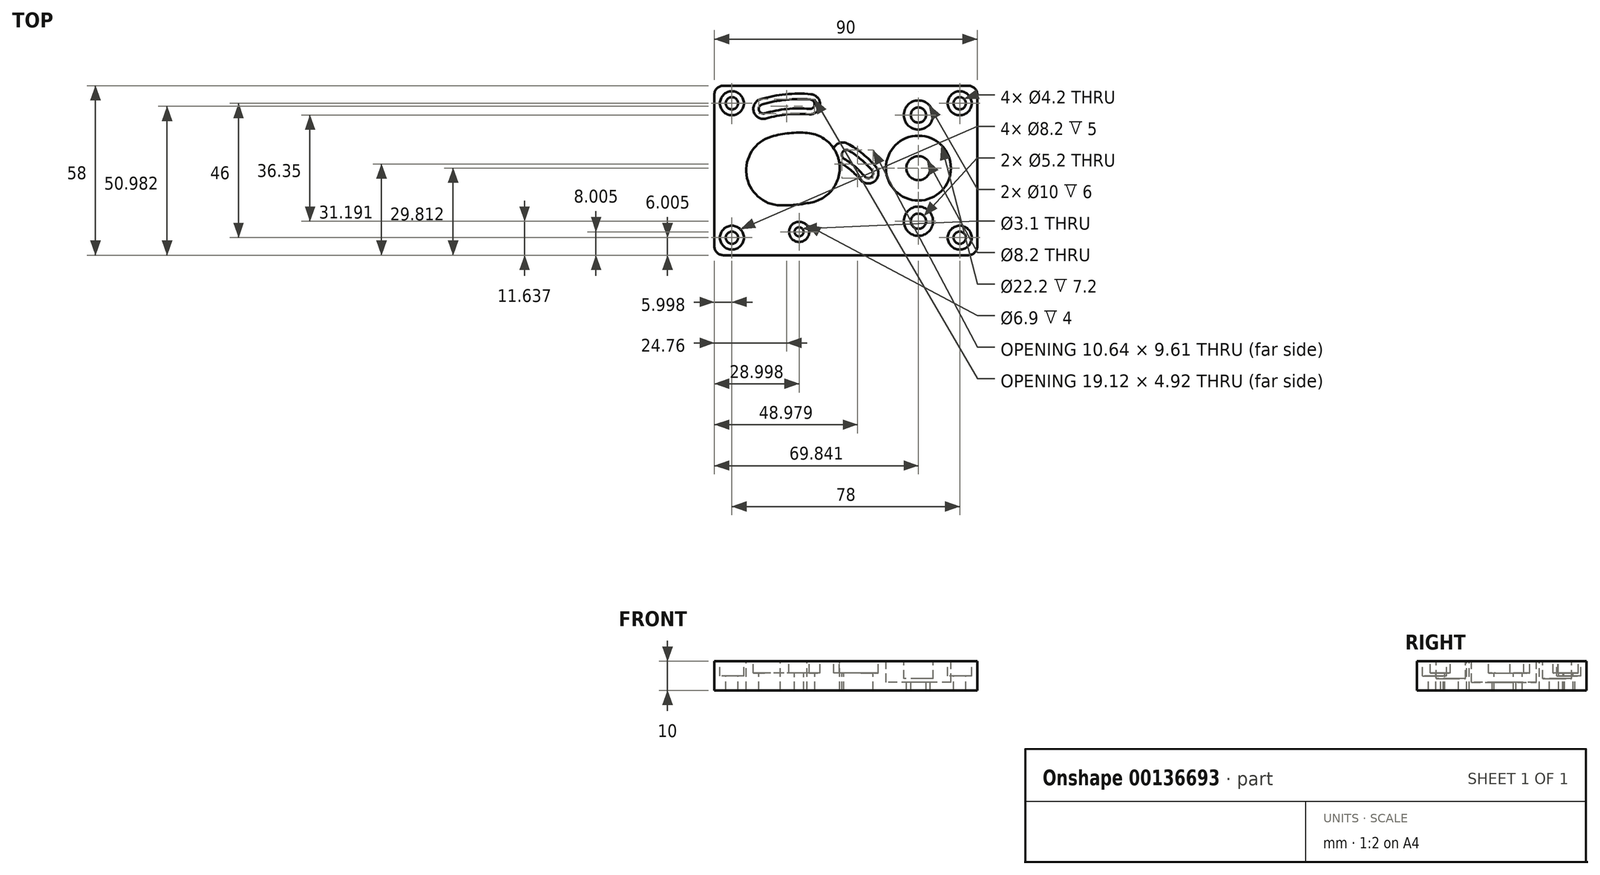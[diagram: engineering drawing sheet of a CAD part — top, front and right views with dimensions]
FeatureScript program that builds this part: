
annotation { "Feature Type Name" : "Feature", "Feature Type Description" : "" }
export const myFeature = defineFeature(function(context is Context, id is Id, definition is map)
    precondition{}
    {
        {
            var Q0;
            Q0=qCreatedBy(makeId("Top.planeOp"),FACE);
            var sketch = newSketch(context, id + "F0", { "sketchPlane" : qUnion([Q0])});
            skLineSegment(sketch, "E0.right", {"start": v(40.3, 23.5) * mm, "end": v(40.3, -28.5) * mm});
            skCircle(sketch, "E1", {"center": v(-20.7, -23.5) * mm, "radius": 1.55 * mm});
            skArc(sketch, "E2", {"start": v(-33.36, 20.15) * mm, "mid": v(-34.45, 18.16) * mm, "end": v(-32.47, 17.07) * mm});
            skArc(sketch, "E3", {"start": v(-17.1, 18.6) * mm, "mid": v(-15.38, 20.05) * mm, "end": v(-16.84, 21.78) * mm});
            skLineSegment(sketch, "E4", {"start": v(-21.13, -22) * mm, "end": v(-20.7, -23.5) * mm});
            skLineSegment(sketch, "E5", {"start": v(-20.7, -23.5) * mm, "end": v(-20.57, -21.95) * mm});
            skArc(sketch, "E6", {"start": v(-17.1, 18.6) * mm, "mid": v(-24.86, 18.54) * mm, "end": v(-32.47, 17.07) * mm});
            skArc(sketch, "E7", {"start": v(-16.84, 21.78) * mm, "mid": v(-25.17, 21.72) * mm, "end": v(-33.36, 20.15) * mm});
            skPoint(sketch, "E8", {"position": v(-22.86, -1.69) * mm});
            skLineSegment(sketch, "E9.trimOffspring", {"start": v(-20.85, -21.95) * mm, "end": v(-20.7, -23.5) * mm});
            skPoint(sketch, "E10.start.orphan", {"position": v(-25.01, 20.12) * mm});
            skArc(sketch, "E11.0", {"start": v(-16.68, 23.62) * mm, "mid": v(-25.35, 23.57) * mm, "end": v(-33.87, 21.92) * mm});
            skArc(sketch, "E11.1", {"start": v(-17.27, 16.75) * mm, "mid": v(-13.54, 19.9) * mm, "end": v(-16.68, 23.62) * mm});
            skArc(sketch, "E11.2", {"start": v(-17.27, 16.75) * mm, "mid": v(-24.68, 16.7) * mm, "end": v(-31.95, 15.3) * mm});
            skArc(sketch, "E11.3", {"start": v(-33.87, 21.92) * mm, "mid": v(-36.23, 17.65) * mm, "end": v(-31.95, 15.3) * mm});
            skLineSegment(sketch, "E12.anchor2", {"start": v(-22.86, -1.69) * mm, "end": v(-44.67, -3.84) * mm, "construction": true});
            skCircle(sketch, "E13", {"center": v(-20.7, -23.5) * mm, "radius": 3.45 * mm});
            skArc(sketch, "E14", {"start": v(-30.15, 9.08) * mm, "mid": v(-38.7, -4) * mm, "end": v(-27.06, -14.44) * mm});
            skArc(sketch, "E15", {"start": v(-17.81, 10.33) * mm, "mid": v(-24.04, 10.3) * mm, "end": v(-30.15, 9.08) * mm});
            skArc(sketch, "E16", {"start": v(-27.06, -14.44) * mm, "mid": v(-22.5, -14.31) * mm, "end": v(-18, -13.65) * mm});
            skPoint(sketch, "E17.center.orphan", {"position": v(-17.7, -1.69) * mm});
            skArc(sketch, "E18.trimOffspring", {"start": v(-18, -13.65) * mm, "mid": v(-6.81, -1.75) * mm, "end": v(-17.81, 10.33) * mm});
            skLineSegment(sketch, "E19", {"start": v(-22.86, -1.69) * mm, "end": v(50.56, -1.69) * mm, "construction": true});
            skCircle(sketch, "E20", {"center": v(20.14, -1.69) * mm, "radius": 4.1 * mm});
            skCircle(sketch, "E21", {"center": v(20.14, -1.69) * mm, "radius": 11.1 * mm});
            skLineSegment(sketch, "E22", {"start": v(-49.7, 23.5) * mm, "end": v(-49.7, -28.5) * mm});
            skLineSegment(sketch, "E23", {"start": v(37.3, 26.5) * mm, "end": v(-46.7, 26.5) * mm});
            skLineSegment(sketch, "E24", {"start": v(37.3, -31.5) * mm, "end": v(-46.7, -31.5) * mm});
            skLineSegment(sketch, "E25", {"start": v(-22.86, -1.69) * mm, "end": v(-55.16, -1.69) * mm, "construction": true});
            skCircle(sketch, "E26", {"center": v(-43.7, 20.5) * mm, "radius": 2.1 * mm});
            skCircle(sketch, "E27", {"center": v(34.3, 20.5) * mm, "radius": 2.1 * mm});
            skCircle(sketch, "E28", {"center": v(-43.7, -25.5) * mm, "radius": 2.1 * mm});
            skCircle(sketch, "E29", {"center": v(34.3, -25.5) * mm, "radius": 2.1 * mm});
            skPoint(sketch, "E30.visualSharp", {"position": v(-49.7, 26.5) * mm});
            skArc(sketch, "E30.filletArc", {"start": v(-46.7, 26.5) * mm, "mid": v(-48.82, 25.63) * mm, "end": v(-49.7, 23.5) * mm});
            skPoint(sketch, "E31.visualSharp", {"position": v(-49.7, -31.5) * mm});
            skArc(sketch, "E31.filletArc", {"start": v(-49.7, -28.5) * mm, "mid": v(-48.82, -30.62) * mm, "end": v(-46.7, -31.5) * mm});
            skPoint(sketch, "E32.visualSharp", {"position": v(40.3, -31.5) * mm});
            skArc(sketch, "E32.filletArc", {"start": v(37.3, -31.5) * mm, "mid": v(39.42, -30.62) * mm, "end": v(40.3, -28.5) * mm});
            skPoint(sketch, "E33.visualSharp", {"position": v(40.3, 26.5) * mm});
            skArc(sketch, "E33.filletArc", {"start": v(40.3, 23.5) * mm, "mid": v(39.42, 25.63) * mm, "end": v(37.3, 26.5) * mm});
            skCircle(sketch, "E34", {"center": v(-43.7, 20.5) * mm, "radius": 4.1 * mm});
            skCircle(sketch, "E35", {"center": v(-43.7, -25.5) * mm, "radius": 4.1 * mm});
            skCircle(sketch, "E36", {"center": v(34.3, -25.5) * mm, "radius": 4.1 * mm});
            skCircle(sketch, "E37", {"center": v(34.3, 20.5) * mm, "radius": 4.1 * mm});
            skLineSegment(sketch, "E38", {"start": v(-20.7, -23.5) * mm, "end": v(-16.97, 20.19) * mm, "construction": true});
            skLineSegment(sketch, "E39", {"start": v(-20.7, -23.5) * mm, "end": v(-32.91, 18.61) * mm, "construction": true});
            skLineSegment(sketch, "E40", {"start": v(-18.84, -1.65) * mm, "end": v(5.84, -3.76) * mm, "construction": true});
            skLineSegment(sketch, "E41", {"start": v(-26.8, -2.44) * mm, "end": v(-1.4, 4.93) * mm, "construction": true});
            skArc(sketch, "E42", {"start": v(1.78, -4.55) * mm, "mid": v(4.04, -4.74) * mm, "end": v(4.23, -2.49) * mm});
            skLineSegment(sketch, "E43", {"start": v(-20.7, -23.5) * mm, "end": v(-5.75, 3.66) * mm, "construction": true});
            skLineSegment(sketch, "E44", {"start": v(3, -3.52) * mm, "end": v(-20.7, -23.5) * mm, "construction": true});
            skLineSegment(sketch, "E45", {"start": v(-5.75, 3.66) * mm, "end": v(-1.87, 10.71) * mm, "construction": true});
            skLineSegment(sketch, "E46", {"start": v(3, -3.52) * mm, "end": v(8.43, 1.05) * mm, "construction": true});
            skArc(sketch, "E47", {"start": v(4.23, -2.49) * mm, "mid": v(0.59, 1.22) * mm, "end": v(-3.62, 4.28) * mm});
            skArc(sketch, "E48", {"start": v(1.78, -4.55) * mm, "mid": v(-1.5, -1.25) * mm, "end": v(-5.25, 1.5) * mm});
            skArc(sketch, "E49.0", {"start": v(5.64, -1.3) * mm, "mid": v(1.15, 3.15) * mm, "end": v(-4.1, 6.68) * mm});
            skArc(sketch, "E49.1", {"start": v(0.37, -5.74) * mm, "mid": v(5.22, -6.15) * mm, "end": v(5.64, -1.3) * mm});
            skArc(sketch, "E49.2", {"start": v(0.37, -5.74) * mm, "mid": v(-3.04, -2.36) * mm, "end": v(-6.98, 0.39) * mm});
            skArc(sketch, "E49.3", {"start": v(-4.1, 6.68) * mm, "mid": v(-6.83, 6.92) * mm, "end": v(-8.87, 5.08) * mm});
            skArc(sketch, "E50", {"start": v(-3.6, 4.28) * mm, "mid": v(-5.81, 3.77) * mm, "end": v(-5.35, 1.56) * mm});
            skPoint(sketch, "E50.first.point", {"position": v(-3.62, 4.28) * mm});
            skPoint(sketch, "E50.second.point", {"position": v(-5.35, 1.56) * mm});
            skPoint(sketch, "E50.third.point", {"position": v(-3.36, 1.72) * mm});
            skLineSegment(sketch, "E51", {"start": v(-5.25, 1.5) * mm, "end": v(-5.35, 1.56) * mm});
            skLineSegment(sketch, "E52", {"start": v(20.14, -1.69) * mm, "end": v(20.14, 24.45) * mm, "construction": true});
            skLineSegment(sketch, "E53", {"start": v(20.14, -1.69) * mm, "end": v(20.14, -26.47) * mm, "construction": true});
            skCircle(sketch, "E54", {"center": v(20.14, -19.86) * mm, "radius": 2.6 * mm});
            skCircle(sketch, "E55", {"center": v(20.14, 16.49) * mm, "radius": 2.6 * mm});
            skCircle(sketch, "E56", {"center": v(20.14, 16.49) * mm, "radius": 5 * mm});
            skCircle(sketch, "E57", {"center": v(20.14, -19.86) * mm, "radius": 5 * mm});
            skSolve(sketch);
        }
        {
            var Q0;
            Q0=makeQuery(id+"F0.imprint","IMPRINT",FACE,{"disambiguationData":[TD([[makeQuery(id+"F0.imprint","IMPRINT",EDGE,{"derivedFrom":sQuery(id+"F0.wireOp",EDGE,"E0.right")}),-1.0]])]});
            var Q1;
            Q1=makeQuery(id+"F0.imprint","IMPRINT",FACE,{"disambiguationData":[TD([[makeQuery(id+"F0.imprint","IMPRINT",EDGE,{"derivedFrom":sQuery(id+"F0.wireOp",EDGE,"E28")}),-1.0]])]});
            var Q2;
            Q2=makeQuery(id+"F0.imprint","IMPRINT",FACE,{"disambiguationData":[TD([[makeQuery(id+"F0.imprint","IMPRINT",EDGE,{"derivedFrom":sQuery(id+"F0.wireOp",EDGE,"E54")}),-1.0]])]});
            var Q3;
            Q3=makeQuery(id+"F0.imprint","IMPRINT",FACE,{"disambiguationData":[TD([[makeQuery(id+"F0.imprint","IMPRINT",EDGE,{"derivedFrom":sQuery(id+"F0.wireOp",EDGE,"E29")}),-1.0]])]});
            var Q4;
            Q4=makeQuery(id+"F0.imprint","IMPRINT",FACE,{"disambiguationData":[TD([[makeQuery(id+"F0.imprint","IMPRINT",EDGE,{"derivedFrom":sQuery(id+"F0.wireOp",EDGE,"E27")}),-1.0]])]});
            var Q5;
            Q5=makeQuery(id+"F0.imprint","IMPRINT",FACE,{"disambiguationData":[TD([[makeQuery(id+"F0.imprint","IMPRINT",EDGE,{"derivedFrom":sQuery(id+"F0.wireOp",EDGE,"E26")}),-1.0]])]});
            var Q6;
            {var subQ5=sQuery(id+"F0.wireOp",EDGE,"E42");Q6=makeQuery(id+"F0.imprint","IMPRINT",FACE,{"disambiguationData":[TD([[makeQuery(id+"F0.imprint","IMPRINT",EDGE,{"derivedFrom":subQ5}),-1.0]])]});}
            var Q7;
            Q7=makeQuery(id+"F0.imprint","IMPRINT",FACE,{"disambiguationData":[TD([[makeQuery(id+"F0.imprint","IMPRINT",EDGE,{"derivedFrom":sQuery(id+"F0.wireOp",EDGE,"E20")}),-1.0]])]});
            var Q8;
            Q8=makeQuery(id+"F0.imprint","IMPRINT",FACE,{"disambiguationData":[TD([[makeQuery(id+"F0.imprint","IMPRINT",EDGE,{"derivedFrom":sQuery(id+"F0.wireOp",EDGE,"E55")}),-1.0]])]});
            var Q9;
            Q9=makeQuery(id+"F0.imprint","IMPRINT",FACE,{"disambiguationData":[TD([[makeQuery(id+"F0.imprint","IMPRINT",EDGE,{"derivedFrom":sQuery(id+"F0.wireOp",EDGE,"E2")}),-1.0]])]});
            extrude(context, id + "F1", {"entities" : qUnion([Q0, Q1, Q2, Q3, Q4, Q5, Q6, Q7, Q8, Q9]), "oppositeDirection" : true, "depth" : 14.97 * mm});
        }
        {
            var Q0;
            Q0=makeQuery(id+"F0.imprint","IMPRINT",FACE,{"disambiguationData":[TD([[makeQuery(id+"F0.imprint","IMPRINT",EDGE,{"derivedFrom":sQuery(id+"F0.wireOp",EDGE,"E20")}),-1.0]])]});
            extrude(context, id + "F2", {"entities" : qUnion([Q0]), "operationType" : NewBodyOperationType.REMOVE, "oppositeDirection" : true, "depth" : 7.2 * mm});
        }
        {
            var Q0;
            Q0=makeQuery(id+"F0.imprint","IMPRINT",FACE,{"disambiguationData":[TD([[makeQuery(id+"F0.imprint","IMPRINT",EDGE,{"derivedFrom":sQuery(id+"F0.wireOp",EDGE,"E13")}),1.0]])]});
            extrude(context, id + "F3", {"entities" : qUnion([Q0]), "operationType" : NewBodyOperationType.ADD, "oppositeDirection" : true, "depth" : 10 * mm});
        }
        {
            var Q0;
            Q0=makeQuery(id+"F0.imprint","IMPRINT",FACE,{"disambiguationData":[TD([[makeQuery(id+"F0.imprint","IMPRINT",EDGE,{"derivedFrom":sQuery(id+"F0.wireOp",EDGE,"E55")}),-1.0]])]});
            var Q1;
            Q1=makeQuery(id+"F0.imprint","IMPRINT",FACE,{"disambiguationData":[TD([[makeQuery(id+"F0.imprint","IMPRINT",EDGE,{"derivedFrom":sQuery(id+"F0.wireOp",EDGE,"E54")}),-1.0]])]});
            extrude(context, id + "F4", {"entities" : qUnion([Q0, Q1]), "operationType" : NewBodyOperationType.REMOVE, "oppositeDirection" : true, "depth" : 6 * mm});
        }
        {
            var Q0;
            Q0=makeQuery(id+"F0.imprint","IMPRINT",FACE,{"disambiguationData":[TD([[makeQuery(id+"F0.imprint","IMPRINT",EDGE,{"derivedFrom":sQuery(id+"F0.wireOp",EDGE,"E26")}),-1.0]])]});
            var Q1;
            Q1=makeQuery(id+"F0.imprint","IMPRINT",FACE,{"disambiguationData":[TD([[makeQuery(id+"F0.imprint","IMPRINT",EDGE,{"derivedFrom":sQuery(id+"F0.wireOp",EDGE,"E28")}),-1.0]])]});
            var Q2;
            Q2=makeQuery(id+"F0.imprint","IMPRINT",FACE,{"disambiguationData":[TD([[makeQuery(id+"F0.imprint","IMPRINT",EDGE,{"derivedFrom":sQuery(id+"F0.wireOp",EDGE,"E27")}),-1.0]])]});
            var Q3;
            Q3=makeQuery(id+"F0.imprint","IMPRINT",FACE,{"disambiguationData":[TD([[makeQuery(id+"F0.imprint","IMPRINT",EDGE,{"derivedFrom":sQuery(id+"F0.wireOp",EDGE,"E29")}),-1.0]])]});
            extrude(context, id + "F5", {"entities" : qUnion([Q0, Q1, Q2, Q3]), "operationType" : NewBodyOperationType.REMOVE, "oppositeDirection" : true, "depth" : 5 * mm});
        }
        {
            var Q0;
            Q0=makeQuery(id+"F0.imprint","IMPRINT",FACE,{"disambiguationData":[TD([[makeQuery(id+"F0.imprint","IMPRINT",EDGE,{"derivedFrom":sQuery(id+"F0.wireOp",EDGE,"E2")}),-1.0]])]});
            var Q1;
            {var subQ5=sQuery(id+"F0.wireOp",EDGE,"E42");Q1=makeQuery(id+"F0.imprint","IMPRINT",FACE,{"disambiguationData":[TD([[makeQuery(id+"F0.imprint","IMPRINT",EDGE,{"derivedFrom":subQ5}),-1.0]])]});}
            var Q2;
            Q2=makeQuery(id+"F0.imprint","IMPRINT",FACE,{"disambiguationData":[TD([[makeQuery(id+"F0.imprint","IMPRINT",EDGE,{"derivedFrom":sQuery(id+"F0.wireOp",EDGE,"E13")}),1.0]])]});
            extrude(context, id + "F6", {"entities" : qUnion([Q0, Q1, Q2]), "operationType" : NewBodyOperationType.REMOVE, "oppositeDirection" : true, "depth" : 4 * mm});
        }
        {
            var Q0;
            Q0=makeQuery(id+"F0.imprint","IMPRINT",FACE,{"disambiguationData":[TD([[makeQuery(id+"F0.imprint","IMPRINT",EDGE,{"derivedFrom":sQuery(id+"F0.wireOp",EDGE,"E13")}),1.0]])]});
            extrude(context, id + "F7", {"entities" : qUnion([Q0]), "operationType" : NewBodyOperationType.ADD, "oppositeDirection" : true, "depth" : 10 * mm});
        }
        {
            var Q0;
            Q0=makeQuery(id+"F1.opExtrude","CAP_FACE",FACE,{"disambiguationData":[OSD([sQuery(id+"F0.wireOp",EDGE,"E0.right"),sQuery(id+"F0.wireOp",EDGE,"E2"),sQuery(id+"F0.wireOp",EDGE,"E3"),sQuery(id+"F0.wireOp",EDGE,"E6"),sQuery(id+"F0.wireOp",EDGE,"E7"),sQuery(id+"F0.wireOp",EDGE,"E13"),sQuery(id+"F0.wireOp",EDGE,"E14"),sQuery(id+"F0.wireOp",EDGE,"E15"),sQuery(id+"F0.wireOp",EDGE,"E16"),sQuery(id+"F0.wireOp",EDGE,"E18.trimOffspring"),sQuery(id+"F0.wireOp",EDGE,"E20"),sQuery(id+"F0.wireOp",EDGE,"E22"),sQuery(id+"F0.wireOp",EDGE,"E23"),sQuery(id+"F0.wireOp",EDGE,"E24"),sQuery(id+"F0.wireOp",EDGE,"E26"),sQuery(id+"F0.wireOp",EDGE,"E27"),sQuery(id+"F0.wireOp",EDGE,"E28"),sQuery(id+"F0.wireOp",EDGE,"E29"),sQuery(id+"F0.wireOp",EDGE,"E30.filletArc"),sQuery(id+"F0.wireOp",EDGE,"E31.filletArc"),sQuery(id+"F0.wireOp",EDGE,"E32.filletArc"),sQuery(id+"F0.wireOp",EDGE,"E33.filletArc"),sQuery(id+"F0.wireOp",EDGE,"E42"),sQuery(id+"F0.wireOp",EDGE,"E47"),sQuery(id+"F0.wireOp",EDGE,"E48"),sQuery(id+"F0.wireOp",EDGE,"E50"),sQuery(id+"F0.wireOp",EDGE,"E51"),sQuery(id+"F0.wireOp",EDGE,"E54"),sQuery(id+"F0.wireOp",EDGE,"E55")])],"isStart":false});
            extrude(context, id + "F8", {"entities" : qUnion([Q0]), "operationType" : NewBodyOperationType.REMOVE, "oppositeDirection" : true, "depth" : 5 * mm});
        }
        {
            var Q0;
            Q0=makeQuery(id+"F0.imprint","IMPRINT",FACE,{"disambiguationData":[TD([[makeQuery(id+"F0.imprint","IMPRINT",EDGE,{"derivedFrom":sQuery(id+"F0.wireOp",EDGE,"E13")}),1.0]])]});
            extrude(context, id + "F9", {"entities" : qUnion([Q0]), "operationType" : NewBodyOperationType.REMOVE, "oppositeDirection" : true, "depth" : 4 * mm});
        }
    });
